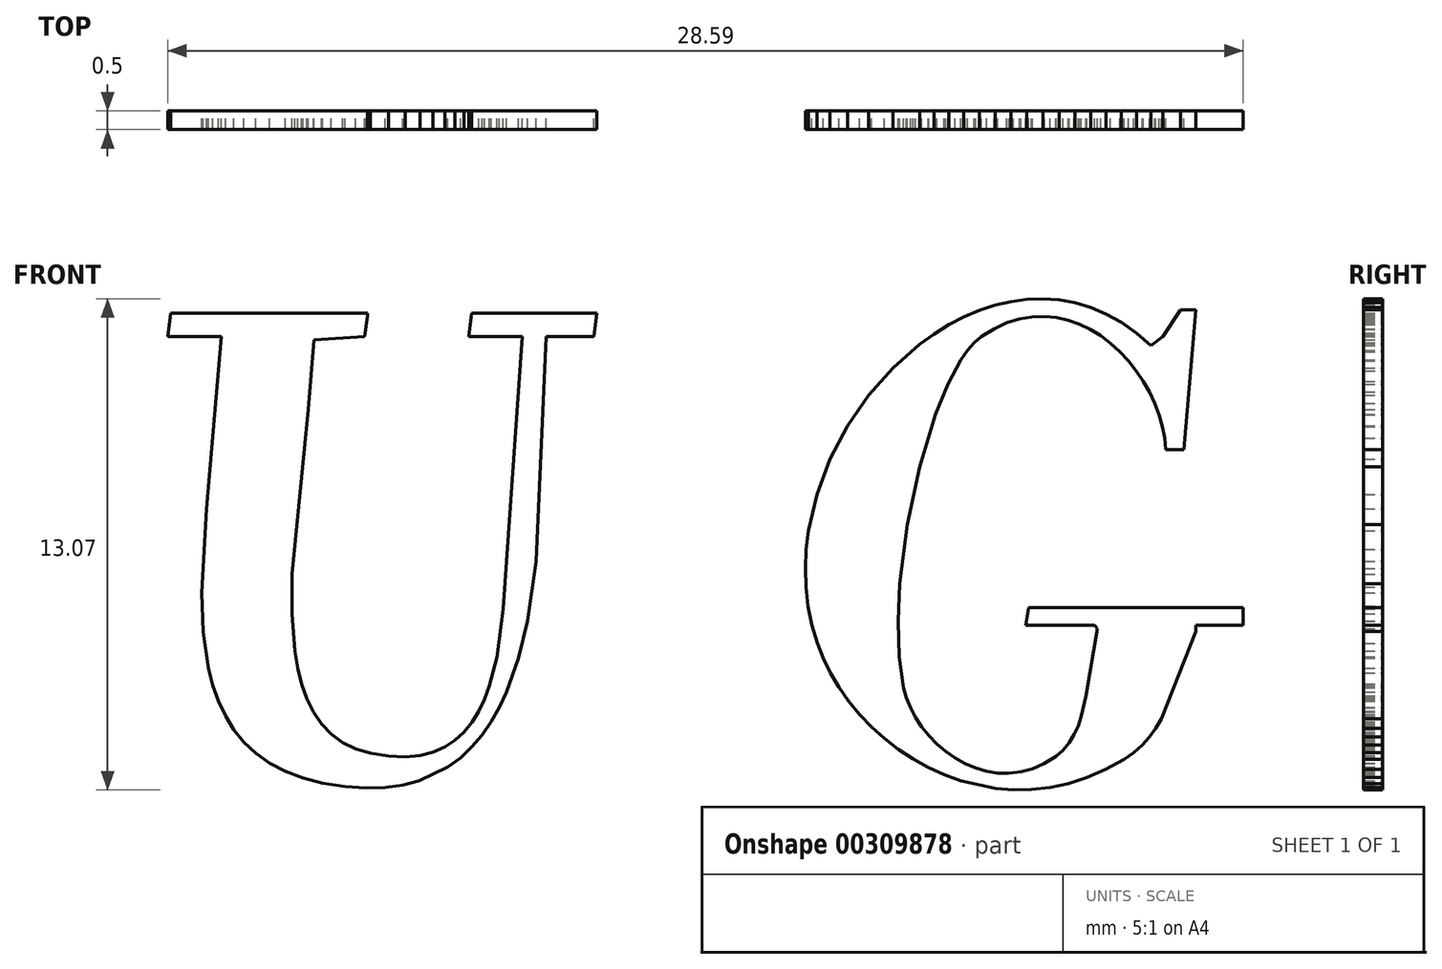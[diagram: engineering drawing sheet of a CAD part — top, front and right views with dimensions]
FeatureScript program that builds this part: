
annotation { "Feature Type Name" : "Feature", "Feature Type Description" : "" }
export const myFeature = defineFeature(function(context is Context, id is Id, definition is map)
    precondition{}
    {
        {
            var Q0;
            Q0=qCreatedBy(makeId("Front.planeOp"),FACE);
            var sketch = newSketch(context, id + "F0", { "sketchPlane" : qUnion([Q0])});
            skPoint(sketch, "E0.0", {"position": v(-16.68, 7.35) * mm});
            skPoint(sketch, "E1.0", {"position": v(-16.76, 6.72) * mm});
            skPoint(sketch, "E2.0", {"position": v(-15.33, 6.72) * mm});
            skPoint(sketch, "E3.0", {"position": v(-11.45, 7.35) * mm});
            skPoint(sketch, "E4.0", {"position": v(-11.45, 7.27) * mm});
            skPoint(sketch, "E5.0", {"position": v(-11.53, 6.72) * mm});
            skPoint(sketch, "E6.0", {"position": v(-12.88, 6.64) * mm});
            skPoint(sketch, "E7.0", {"position": v(-13.02, 4.78) * mm});
            skPoint(sketch, "E8.0", {"position": v(-13.46, 0.4) * mm});
            skPoint(sketch, "E9.0", {"position": v(-15.73, 2.14) * mm});
            skPoint(sketch, "E10.0", {"position": v(-15.86, -0.1) * mm});
            skPoint(sketch, "E11.0", {"position": v(-15.82, -1.14) * mm});
            skPoint(sketch, "E12.0", {"position": v(-13.46, -0.66) * mm});
            skPoint(sketch, "E13.0", {"position": v(-13.39, -1.64) * mm});
            skPoint(sketch, "E14.0", {"position": v(-15.68, -2.1) * mm});
            skPoint(sketch, "E15.0", {"position": v(-15.56, -2.55) * mm});
            skPoint(sketch, "E16.0", {"position": v(-13.3, -2.1) * mm});
            skPoint(sketch, "E17.0", {"position": v(-13.2, -2.52) * mm});
            skPoint(sketch, "E18.0", {"position": v(-15.41, -2.98) * mm});
            skPoint(sketch, "E19.0", {"position": v(-15.23, -3.37) * mm});
            skPoint(sketch, "E20.0", {"position": v(-13.06, -2.92) * mm});
            skPoint(sketch, "E21.0", {"position": v(-15, -3.74) * mm});
            skPoint(sketch, "E22.0", {"position": v(-14.73, -4.07) * mm});
            skPoint(sketch, "E23.0", {"position": v(-14.42, -4.37) * mm});
            skPoint(sketch, "E24.0", {"position": v(-14.05, -4.63) * mm});
            skPoint(sketch, "E25.0", {"position": v(-13.64, -4.85) * mm});
            skPoint(sketch, "E26.0", {"position": v(-13.17, -5.03) * mm});
            skPoint(sketch, "E27.0", {"position": v(-12.64, -5.16) * mm});
            skPoint(sketch, "E28.0", {"position": v(-12.88, -3.27) * mm});
            skPoint(sketch, "E29.0", {"position": v(-12.67, -3.59) * mm});
            skPoint(sketch, "E30.0", {"position": v(-12.41, -3.86) * mm});
            skPoint(sketch, "E31.0", {"position": v(-12.11, -4.08) * mm});
            skPoint(sketch, "E32.0", {"position": v(-12.05, -5.26) * mm});
            skPoint(sketch, "E33.0", {"position": v(-11.77, -4.25) * mm});
            skPoint(sketch, "E34.0", {"position": v(-11.5, -5.3) * mm});
            skPoint(sketch, "E35.0", {"position": v(-11.37, -4.37) * mm});
            skPoint(sketch, "E36.0", {"position": v(-10.89, -4.44) * mm});
            skPoint(sketch, "E37.0", {"position": v(-10.98, -5.28) * mm});
            skPoint(sketch, "E38.0", {"position": v(-10.45, -4.46) * mm});
            skPoint(sketch, "E39.0", {"position": v(-10.51, -5.21) * mm});
            skPoint(sketch, "E40.0", {"position": v(-10.08, -5.1) * mm});
            skPoint(sketch, "E41.0", {"position": v(-10.06, -4.42) * mm});
            skPoint(sketch, "E42.0", {"position": v(-9.7, -4.34) * mm});
            skPoint(sketch, "E43.0", {"position": v(-9.31, -4.73) * mm});
            skPoint(sketch, "E44.0", {"position": v(-9.4, -4.2) * mm});
            skPoint(sketch, "E45.0", {"position": v(-8.98, -4.49) * mm});
            skPoint(sketch, "E46.0", {"position": v(-9.12, -4.02) * mm});
            skPoint(sketch, "E47.0", {"position": v(-8.68, -4.2) * mm});
            skPoint(sketch, "E48.0", {"position": v(-8.88, -3.8) * mm});
            skPoint(sketch, "E49.0", {"position": v(-8.4, -3.88) * mm});
            skPoint(sketch, "E50.0", {"position": v(-8.67, -3.54) * mm});
            skPoint(sketch, "E51.0", {"position": v(-8.16, -3.53) * mm});
            skPoint(sketch, "E52.0", {"position": v(-8.5, -3.25) * mm});
            skPoint(sketch, "E53.0", {"position": v(-7.95, -3.15) * mm});
            skPoint(sketch, "E54.0", {"position": v(-8.34, -2.93) * mm});
            skPoint(sketch, "E55.0", {"position": v(-8.2, -2.58) * mm});
            skPoint(sketch, "E56.0", {"position": v(-7.75, -2.73) * mm});
            skPoint(sketch, "E57.0", {"position": v(-8.02, -1.8) * mm});
            skPoint(sketch, "E58.0", {"position": v(-7.44, -1.83) * mm});
            skPoint(sketch, "E59.0", {"position": v(-7.2, -0.85) * mm});
            skPoint(sketch, "E60.0", {"position": v(-7.85, -0.53) * mm});
            skPoint(sketch, "E61.0", {"position": v(-6.96, 0.75) * mm});
            skPoint(sketch, "E62.0", {"position": v(-6.7, 6.72) * mm});
            skPoint(sketch, "E63.0", {"position": v(-7.33, 6.72) * mm});
            skPoint(sketch, "E64.0", {"position": v(-8.76, 6.72) * mm});
            skPoint(sketch, "E65.0", {"position": v(-8.68, 7.35) * mm});
            skPoint(sketch, "E66.0", {"position": v(-5.35, 7.35) * mm});
            skPoint(sketch, "E67.0", {"position": v(-5.43, 6.72) * mm});
            skPoint(sketch, "E68.0", {"position": v(10.57, 7.43) * mm});
            skPoint(sketch, "E69.0", {"position": v(10.25, 3.7) * mm});
            skPoint(sketch, "E70.0", {"position": v(9.77, 3.7) * mm});
            skPoint(sketch, "E71.0", {"position": v(9.74, 4.02) * mm});
            skPoint(sketch, "E72.0", {"position": v(9.68, 4.33) * mm});
            skPoint(sketch, "E73.0", {"position": v(9.6, 4.64) * mm});
            skPoint(sketch, "E74.0", {"position": v(9.48, 4.95) * mm});
            skPoint(sketch, "E75.0", {"position": v(9.33, 5.25) * mm});
            skPoint(sketch, "E76.0", {"position": v(9.17, 5.54) * mm});
            skPoint(sketch, "E77.0", {"position": v(8.98, 5.82) * mm});
            skPoint(sketch, "E78.0", {"position": v(8.77, 6.08) * mm});
            skPoint(sketch, "E79.0", {"position": v(10.17, 7.43) * mm});
            skPoint(sketch, "E80.0", {"position": v(9.7, 6.72) * mm});
            skPoint(sketch, "E81.0", {"position": v(9.38, 6.48) * mm});
            skPoint(sketch, "E82.0", {"position": v(9, 6.82) * mm});
            skPoint(sketch, "E83.0", {"position": v(8.55, 6.32) * mm});
            skPoint(sketch, "E84.0", {"position": v(8.3, 6.55) * mm});
            skPoint(sketch, "E85.0", {"position": v(8.6, 7.1) * mm});
            skPoint(sketch, "E86.0", {"position": v(8.19, 7.33) * mm});
            skPoint(sketch, "E87.0", {"position": v(7.77, 6.91) * mm});
            skPoint(sketch, "E88.0", {"position": v(8.04, 6.74) * mm});
            skPoint(sketch, "E89.0", {"position": v(7.78, 7.5) * mm});
            skPoint(sketch, "E90.0", {"position": v(7.48, 7.05) * mm});
            skPoint(sketch, "E91.0", {"position": v(7.36, 7.63) * mm});
            skPoint(sketch, "E92.0", {"position": v(7.18, 7.16) * mm});
            skPoint(sketch, "E93.0", {"position": v(6.87, 7.23) * mm});
            skPoint(sketch, "E94.0", {"position": v(6.93, 7.7) * mm});
            skPoint(sketch, "E95.0", {"position": v(6.5, 7.73) * mm});
            skPoint(sketch, "E96.0", {"position": v(6.55, 7.26) * mm});
            skPoint(sketch, "E97.0", {"position": v(6.22, 7.25) * mm});
            skPoint(sketch, "E98.0", {"position": v(6.08, 7.71) * mm});
            skPoint(sketch, "E99.0", {"position": v(5.65, 7.66) * mm});
            skPoint(sketch, "E100.0", {"position": v(5.88, 7.2) * mm});
            skPoint(sketch, "E101.0", {"position": v(5.23, 7.56) * mm});
            skPoint(sketch, "E102.0", {"position": v(5.55, 7.09) * mm});
            skPoint(sketch, "E103.0", {"position": v(5.2, 6.93) * mm});
            skPoint(sketch, "E104.0", {"position": v(4.82, 7.42) * mm});
            skPoint(sketch, "E105.0", {"position": v(4.4, 7.25) * mm});
            skPoint(sketch, "E106.0", {"position": v(4.86, 6.72) * mm});
            skPoint(sketch, "E107.0", {"position": v(4.68, 6.56) * mm});
            skPoint(sketch, "E108.0", {"position": v(4, 7.04) * mm});
            skPoint(sketch, "E109.0", {"position": v(3.61, 6.8) * mm});
            skPoint(sketch, "E110.0", {"position": v(4.32, 6.1) * mm});
            skPoint(sketch, "E111.0", {"position": v(4.5, 6.36) * mm});
            skPoint(sketch, "E112.0", {"position": v(3.23, 6.52) * mm});
            skPoint(sketch, "E113.0", {"position": v(3.98, 5.45) * mm});
            skPoint(sketch, "E114.0", {"position": v(2.52, 5.89) * mm});
            skPoint(sketch, "E115.0", {"position": v(3.66, 4.65) * mm});
            skPoint(sketch, "E116.0", {"position": v(1.87, 5.16) * mm});
            skPoint(sketch, "E117.0", {"position": v(3.23, 3.26) * mm});
            skPoint(sketch, "E118.0", {"position": v(1.3, 4.34) * mm});
            skPoint(sketch, "E119.0", {"position": v(0.84, 3.46) * mm});
            skPoint(sketch, "E120.0", {"position": v(2.9, 1.72) * mm});
            skPoint(sketch, "E121.0", {"position": v(0.5, 2.52) * mm});
            skPoint(sketch, "E122.0", {"position": v(0.27, 1.55) * mm});
            skPoint(sketch, "E123.0", {"position": v(2.7, 0.15) * mm});
            skPoint(sketch, "E124.0", {"position": v(0.21, 1.05) * mm});
            skPoint(sketch, "E125.0", {"position": v(0.19, 0.55) * mm});
            skPoint(sketch, "E126.0", {"position": v(0.2, 0.05) * mm});
            skPoint(sketch, "E127.0", {"position": v(2.65, -0.86) * mm});
            skPoint(sketch, "E128.0", {"position": v(0.26, -0.45) * mm});
            skPoint(sketch, "E129.0", {"position": v(0.36, -0.94) * mm});
            skPoint(sketch, "E130.0", {"position": v(0.5, -1.44) * mm});
            skPoint(sketch, "E131.0", {"position": v(0.67, -1.84) * mm});
            skPoint(sketch, "E132.0", {"position": v(2.69, -1.8) * mm});
            skPoint(sketch, "E133.0", {"position": v(0.86, -2.23) * mm});
            skPoint(sketch, "E134.0", {"position": v(1.09, -2.62) * mm});
            skPoint(sketch, "E135.0", {"position": v(1.34, -2.98) * mm});
            skPoint(sketch, "E136.0", {"position": v(1.63, -3.33) * mm});
            skPoint(sketch, "E137.0", {"position": v(2.88, -2.9) * mm});
            skPoint(sketch, "E138.0", {"position": v(2.8, -2.63) * mm});
            skPoint(sketch, "E139.0", {"position": v(2.98, -3.16) * mm});
            skPoint(sketch, "E140.0", {"position": v(1.95, -3.66) * mm});
            skPoint(sketch, "E141.0", {"position": v(2.3, -3.97) * mm});
            skPoint(sketch, "E142.0", {"position": v(3.12, -3.41) * mm});
            skPoint(sketch, "E143.0", {"position": v(3.29, -3.66) * mm});
            skPoint(sketch, "E144.0", {"position": v(2.66, -4.26) * mm});
            skPoint(sketch, "E145.0", {"position": v(3.47, -3.9) * mm});
            skPoint(sketch, "E146.0", {"position": v(3.05, -4.52) * mm});
            skPoint(sketch, "E147.0", {"position": v(3.69, -4.12) * mm});
            skPoint(sketch, "E148.0", {"position": v(3.45, -4.74) * mm});
            skPoint(sketch, "E149.0", {"position": v(3.92, -4.32) * mm});
            skPoint(sketch, "E150.0", {"position": v(3.88, -4.94) * mm});
            skPoint(sketch, "E151.0", {"position": v(4.17, -4.5) * mm});
            skPoint(sketch, "E152.0", {"position": v(4.32, -5.1) * mm});
            skPoint(sketch, "E153.0", {"position": v(4.43, -4.64) * mm});
            skPoint(sketch, "E154.0", {"position": v(5, -4.84) * mm});
            skPoint(sketch, "E155.0", {"position": v(4.71, -4.76) * mm});
            skPoint(sketch, "E156.0", {"position": v(5.24, -5.3) * mm});
            skPoint(sketch, "E157.0", {"position": v(5.3, -4.9) * mm});
            skPoint(sketch, "E158.0", {"position": v(5.6, -4.9) * mm});
            skPoint(sketch, "E159.0", {"position": v(5.72, -5.34) * mm});
            skPoint(sketch, "E160.0", {"position": v(5.92, -4.86) * mm});
            skPoint(sketch, "E161.0", {"position": v(6.2, -5.33) * mm});
            skPoint(sketch, "E162.0", {"position": v(6.23, -4.78) * mm});
            skPoint(sketch, "E163.0", {"position": v(6.7, -5.28) * mm});
            skPoint(sketch, "E164.0", {"position": v(6.54, -4.64) * mm});
            skPoint(sketch, "E165.0", {"position": v(7.19, -5.17) * mm});
            skPoint(sketch, "E166.0", {"position": v(6.84, -4.45) * mm});
            skPoint(sketch, "E167.0", {"position": v(7.68, -5.01) * mm});
            skPoint(sketch, "E168.0", {"position": v(7.04, -4.28) * mm});
            skPoint(sketch, "E169.0", {"position": v(7.2, -4.09) * mm});
            skPoint(sketch, "E170.0", {"position": v(8.17, -4.8) * mm});
            skPoint(sketch, "E171.0", {"position": v(7.33, -3.87) * mm});
            skPoint(sketch, "E172.0", {"position": v(8.66, -4.53) * mm});
            skPoint(sketch, "E173.0", {"position": v(7.44, -3.64) * mm});
            skPoint(sketch, "E174.0", {"position": v(7.53, -3.39) * mm});
            skPoint(sketch, "E175.0", {"position": v(8.92, -4.35) * mm});
            skPoint(sketch, "E176.0", {"position": v(9.15, -4.15) * mm});
            skPoint(sketch, "E177.0", {"position": v(9.34, -3.93) * mm});
            skPoint(sketch, "E178.0", {"position": v(9.5, -3.7) * mm});
            skPoint(sketch, "E179.0", {"position": v(7.65, -2.84) * mm});
            skPoint(sketch, "E180.0", {"position": v(9.65, -3.45) * mm});
            skPoint(sketch, "E181.0", {"position": v(7.95, -1.04) * mm});
            skPoint(sketch, "E182.0", {"position": v(7.87, -0.96) * mm});
            skPoint(sketch, "E183.0", {"position": v(6.05, -0.96) * mm});
            skPoint(sketch, "E184.0", {"position": v(6.13, -0.49) * mm});
            skPoint(sketch, "E185.0", {"position": v(11.83, -0.49) * mm});
            skPoint(sketch, "E186.0", {"position": v(11.83, -0.96) * mm});
            skPoint(sketch, "E187.0", {"position": v(10.57, -0.96) * mm});
            skPoint(sketch, "E188.0", {"position": v(10.57, -1.12) * mm});
            skLineSegment(sketch, "E189", {"start": v(-16.68, 7.35) * mm, "end": v(-11.45, 7.35) * mm});
            skLineSegment(sketch, "E190", {"start": v(-11.45, 7.35) * mm, "end": v(-11.45, 7.27) * mm});
            skLineSegment(sketch, "E191", {"start": v(-11.45, 7.27) * mm, "end": v(-11.53, 6.72) * mm});
            skLineSegment(sketch, "E192", {"start": v(-11.53, 6.72) * mm, "end": v(-12.88, 6.64) * mm});
            skLineSegment(sketch, "E193", {"start": v(-12.88, 6.64) * mm, "end": v(-13.02, 4.78) * mm});
            skLineSegment(sketch, "E194", {"start": v(-13.02, 4.78) * mm, "end": v(-13.46, 0.4) * mm});
            skLineSegment(sketch, "E195", {"start": v(-13.46, 0.4) * mm, "end": v(-13.46, -0.66) * mm});
            skLineSegment(sketch, "E196", {"start": v(-13.46, -0.66) * mm, "end": v(-13.39, -1.64) * mm});
            skLineSegment(sketch, "E197", {"start": v(-13.39, -1.64) * mm, "end": v(-13.3, -2.1) * mm});
            skLineSegment(sketch, "E198", {"start": v(-13.3, -2.1) * mm, "end": v(-13.2, -2.52) * mm});
            skLineSegment(sketch, "E199", {"start": v(-13.2, -2.52) * mm, "end": v(-13.06, -2.92) * mm});
            skLineSegment(sketch, "E200", {"start": v(-13.06, -2.92) * mm, "end": v(-12.88, -3.27) * mm});
            skLineSegment(sketch, "E201", {"start": v(-12.88, -3.27) * mm, "end": v(-12.67, -3.59) * mm});
            skLineSegment(sketch, "E202", {"start": v(-12.67, -3.59) * mm, "end": v(-12.41, -3.86) * mm});
            skLineSegment(sketch, "E203", {"start": v(-12.41, -3.86) * mm, "end": v(-12.11, -4.08) * mm});
            skLineSegment(sketch, "E204", {"start": v(-12.11, -4.08) * mm, "end": v(-11.77, -4.25) * mm});
            skLineSegment(sketch, "E205", {"start": v(-11.77, -4.25) * mm, "end": v(-11.37, -4.37) * mm});
            skLineSegment(sketch, "E206", {"start": v(-11.37, -4.37) * mm, "end": v(-10.89, -4.44) * mm});
            skLineSegment(sketch, "E207", {"start": v(-10.89, -4.44) * mm, "end": v(-10.45, -4.46) * mm});
            skLineSegment(sketch, "E208", {"start": v(-10.45, -4.46) * mm, "end": v(-10.06, -4.42) * mm});
            skLineSegment(sketch, "E209", {"start": v(-10.06, -4.42) * mm, "end": v(-9.7, -4.34) * mm});
            skLineSegment(sketch, "E210", {"start": v(-9.7, -4.34) * mm, "end": v(-9.4, -4.2) * mm});
            skLineSegment(sketch, "E211", {"start": v(-9.4, -4.2) * mm, "end": v(-9.12, -4.02) * mm});
            skLineSegment(sketch, "E212", {"start": v(-9.12, -4.02) * mm, "end": v(-8.88, -3.8) * mm});
            skLineSegment(sketch, "E213", {"start": v(-8.88, -3.8) * mm, "end": v(-8.67, -3.54) * mm});
            skLineSegment(sketch, "E214", {"start": v(-8.67, -3.54) * mm, "end": v(-8.5, -3.25) * mm});
            skLineSegment(sketch, "E215", {"start": v(-8.5, -3.25) * mm, "end": v(-8.34, -2.93) * mm});
            skLineSegment(sketch, "E216", {"start": v(-8.34, -2.93) * mm, "end": v(-8.2, -2.58) * mm});
            skLineSegment(sketch, "E217", {"start": v(-8.2, -2.58) * mm, "end": v(-8.02, -1.8) * mm});
            skLineSegment(sketch, "E218", {"start": v(-8.02, -1.8) * mm, "end": v(-7.85, -0.53) * mm});
            skLineSegment(sketch, "E219", {"start": v(-7.85, -0.53) * mm, "end": v(-7.33, 6.72) * mm});
            skLineSegment(sketch, "E220", {"start": v(-7.33, 6.72) * mm, "end": v(-8.76, 6.72) * mm});
            skLineSegment(sketch, "E221", {"start": v(-8.76, 6.72) * mm, "end": v(-8.68, 7.35) * mm});
            skLineSegment(sketch, "E222", {"start": v(-8.68, 7.35) * mm, "end": v(-5.35, 7.35) * mm});
            skLineSegment(sketch, "E223", {"start": v(-5.35, 7.35) * mm, "end": v(-5.43, 6.72) * mm});
            skLineSegment(sketch, "E224", {"start": v(-5.43, 6.72) * mm, "end": v(-6.7, 6.72) * mm});
            skLineSegment(sketch, "E225", {"start": v(-6.7, 6.72) * mm, "end": v(-6.96, 0.75) * mm});
            skLineSegment(sketch, "E226", {"start": v(-6.96, 0.75) * mm, "end": v(-7.2, -0.85) * mm});
            skLineSegment(sketch, "E227", {"start": v(-7.2, -0.85) * mm, "end": v(-7.44, -1.83) * mm});
            skLineSegment(sketch, "E228", {"start": v(-7.44, -1.83) * mm, "end": v(-7.75, -2.73) * mm});
            skLineSegment(sketch, "E229", {"start": v(-7.75, -2.73) * mm, "end": v(-7.95, -3.15) * mm});
            skLineSegment(sketch, "E230", {"start": v(-7.95, -3.15) * mm, "end": v(-8.16, -3.53) * mm});
            skLineSegment(sketch, "E231", {"start": v(-8.16, -3.53) * mm, "end": v(-8.4, -3.88) * mm});
            skLineSegment(sketch, "E232", {"start": v(-8.4, -3.88) * mm, "end": v(-8.68, -4.2) * mm});
            skLineSegment(sketch, "E233", {"start": v(-8.68, -4.2) * mm, "end": v(-8.98, -4.49) * mm});
            skLineSegment(sketch, "E234", {"start": v(-8.98, -4.49) * mm, "end": v(-9.31, -4.73) * mm});
            skLineSegment(sketch, "E235", {"start": v(-9.31, -4.73) * mm, "end": v(-10.08, -5.1) * mm});
            skLineSegment(sketch, "E236", {"start": v(-10.08, -5.1) * mm, "end": v(-10.51, -5.21) * mm});
            skLineSegment(sketch, "E237", {"start": v(-10.51, -5.21) * mm, "end": v(-10.98, -5.28) * mm});
            skLineSegment(sketch, "E238", {"start": v(-10.98, -5.28) * mm, "end": v(-11.5, -5.3) * mm});
            skLineSegment(sketch, "E239", {"start": v(-11.5, -5.3) * mm, "end": v(-12.05, -5.26) * mm});
            skLineSegment(sketch, "E240", {"start": v(-12.05, -5.26) * mm, "end": v(-12.64, -5.16) * mm});
            skLineSegment(sketch, "E241", {"start": v(-12.64, -5.16) * mm, "end": v(-13.17, -5.03) * mm});
            skLineSegment(sketch, "E242", {"start": v(-13.17, -5.03) * mm, "end": v(-13.64, -4.85) * mm});
            skLineSegment(sketch, "E243", {"start": v(-13.64, -4.85) * mm, "end": v(-14.05, -4.63) * mm});
            skLineSegment(sketch, "E244", {"start": v(-14.05, -4.63) * mm, "end": v(-14.42, -4.37) * mm});
            skLineSegment(sketch, "E245", {"start": v(-14.42, -4.37) * mm, "end": v(-14.73, -4.07) * mm});
            skLineSegment(sketch, "E246", {"start": v(-14.73, -4.07) * mm, "end": v(-15, -3.74) * mm});
            skLineSegment(sketch, "E247", {"start": v(-15, -3.74) * mm, "end": v(-15.23, -3.37) * mm});
            skLineSegment(sketch, "E248", {"start": v(-15.23, -3.37) * mm, "end": v(-15.41, -2.98) * mm});
            skLineSegment(sketch, "E249", {"start": v(-15.41, -2.98) * mm, "end": v(-15.56, -2.55) * mm});
            skLineSegment(sketch, "E250", {"start": v(-15.56, -2.55) * mm, "end": v(-15.68, -2.1) * mm});
            skLineSegment(sketch, "E251", {"start": v(-15.68, -2.1) * mm, "end": v(-15.82, -1.14) * mm});
            skLineSegment(sketch, "E252", {"start": v(-15.82, -1.14) * mm, "end": v(-15.86, -0.1) * mm});
            skLineSegment(sketch, "E253", {"start": v(-15.86, -0.1) * mm, "end": v(-15.73, 2.14) * mm});
            skLineSegment(sketch, "E254", {"start": v(-15.73, 2.14) * mm, "end": v(-15.33, 6.72) * mm});
            skLineSegment(sketch, "E255", {"start": v(-15.33, 6.72) * mm, "end": v(-16.76, 6.72) * mm});
            skLineSegment(sketch, "E256", {"start": v(-16.76, 6.72) * mm, "end": v(-16.68, 7.35) * mm});
            skLineSegment(sketch, "E257", {"start": v(10.57, 7.43) * mm, "end": v(10.25, 3.7) * mm});
            skLineSegment(sketch, "E258", {"start": v(10.25, 3.7) * mm, "end": v(9.77, 3.7) * mm});
            skLineSegment(sketch, "E259", {"start": v(9.77, 3.7) * mm, "end": v(9.74, 4.02) * mm});
            skLineSegment(sketch, "E260", {"start": v(9.74, 4.02) * mm, "end": v(9.68, 4.33) * mm});
            skLineSegment(sketch, "E261", {"start": v(9.68, 4.33) * mm, "end": v(9.6, 4.64) * mm});
            skLineSegment(sketch, "E262", {"start": v(9.6, 4.64) * mm, "end": v(9.48, 4.95) * mm});
            skLineSegment(sketch, "E263", {"start": v(9.48, 4.95) * mm, "end": v(9.33, 5.25) * mm});
            skLineSegment(sketch, "E264", {"start": v(9.33, 5.25) * mm, "end": v(9.17, 5.54) * mm});
            skLineSegment(sketch, "E265", {"start": v(9.17, 5.54) * mm, "end": v(8.98, 5.82) * mm});
            skLineSegment(sketch, "E266", {"start": v(8.98, 5.82) * mm, "end": v(8.77, 6.08) * mm});
            skLineSegment(sketch, "E267", {"start": v(8.77, 6.08) * mm, "end": v(8.55, 6.32) * mm});
            skLineSegment(sketch, "E268", {"start": v(8.55, 6.32) * mm, "end": v(8.3, 6.55) * mm});
            skLineSegment(sketch, "E269", {"start": v(8.3, 6.55) * mm, "end": v(8.04, 6.74) * mm});
            skLineSegment(sketch, "E270", {"start": v(8.04, 6.74) * mm, "end": v(7.77, 6.91) * mm});
            skLineSegment(sketch, "E271", {"start": v(7.77, 6.91) * mm, "end": v(7.48, 7.05) * mm});
            skLineSegment(sketch, "E272", {"start": v(7.48, 7.05) * mm, "end": v(7.18, 7.16) * mm});
            skLineSegment(sketch, "E273", {"start": v(7.18, 7.16) * mm, "end": v(6.87, 7.23) * mm});
            skLineSegment(sketch, "E274", {"start": v(6.87, 7.23) * mm, "end": v(6.55, 7.26) * mm});
            skLineSegment(sketch, "E275", {"start": v(6.55, 7.26) * mm, "end": v(6.22, 7.25) * mm});
            skLineSegment(sketch, "E276", {"start": v(6.22, 7.25) * mm, "end": v(5.88, 7.2) * mm});
            skLineSegment(sketch, "E277", {"start": v(5.88, 7.2) * mm, "end": v(5.55, 7.09) * mm});
            skLineSegment(sketch, "E278", {"start": v(5.55, 7.09) * mm, "end": v(5.2, 6.93) * mm});
            skLineSegment(sketch, "E279", {"start": v(5.2, 6.93) * mm, "end": v(4.86, 6.72) * mm});
            skLineSegment(sketch, "E280", {"start": v(4.86, 6.72) * mm, "end": v(4.68, 6.56) * mm});
            skLineSegment(sketch, "E281", {"start": v(4.68, 6.56) * mm, "end": v(4.5, 6.36) * mm});
            skLineSegment(sketch, "E282", {"start": v(4.5, 6.36) * mm, "end": v(4.32, 6.1) * mm});
            skLineSegment(sketch, "E283", {"start": v(4.32, 6.1) * mm, "end": v(3.98, 5.45) * mm});
            skLineSegment(sketch, "E284", {"start": v(3.98, 5.45) * mm, "end": v(3.66, 4.65) * mm});
            skLineSegment(sketch, "E285", {"start": v(3.66, 4.65) * mm, "end": v(3.23, 3.26) * mm});
            skLineSegment(sketch, "E286", {"start": v(3.23, 3.26) * mm, "end": v(2.9, 1.72) * mm});
            skLineSegment(sketch, "E287", {"start": v(2.9, 1.72) * mm, "end": v(2.7, 0.15) * mm});
            skLineSegment(sketch, "E288", {"start": v(2.7, 0.15) * mm, "end": v(2.65, -0.86) * mm});
            skLineSegment(sketch, "E289", {"start": v(2.65, -0.86) * mm, "end": v(2.69, -1.8) * mm});
            skLineSegment(sketch, "E290", {"start": v(2.69, -1.8) * mm, "end": v(2.8, -2.63) * mm});
            skLineSegment(sketch, "E291", {"start": v(2.8, -2.63) * mm, "end": v(2.88, -2.9) * mm});
            skLineSegment(sketch, "E292", {"start": v(2.88, -2.9) * mm, "end": v(2.98, -3.16) * mm});
            skLineSegment(sketch, "E293", {"start": v(2.98, -3.16) * mm, "end": v(3.12, -3.41) * mm});
            skLineSegment(sketch, "E294", {"start": v(3.12, -3.41) * mm, "end": v(3.29, -3.66) * mm});
            skLineSegment(sketch, "E295", {"start": v(3.29, -3.66) * mm, "end": v(3.47, -3.9) * mm});
            skLineSegment(sketch, "E296", {"start": v(3.47, -3.9) * mm, "end": v(3.69, -4.12) * mm});
            skLineSegment(sketch, "E297", {"start": v(3.69, -4.12) * mm, "end": v(3.92, -4.32) * mm});
            skLineSegment(sketch, "E298", {"start": v(3.92, -4.32) * mm, "end": v(4.17, -4.5) * mm});
            skLineSegment(sketch, "E299", {"start": v(4.17, -4.5) * mm, "end": v(4.43, -4.64) * mm});
            skLineSegment(sketch, "E300", {"start": v(4.43, -4.64) * mm, "end": v(4.71, -4.76) * mm});
            skLineSegment(sketch, "E301", {"start": v(4.71, -4.76) * mm, "end": v(5, -4.84) * mm});
            skLineSegment(sketch, "E302", {"start": v(5, -4.84) * mm, "end": v(5.3, -4.9) * mm});
            skLineSegment(sketch, "E303", {"start": v(5.3, -4.9) * mm, "end": v(5.6, -4.9) * mm});
            skLineSegment(sketch, "E304", {"start": v(5.6, -4.9) * mm, "end": v(5.92, -4.86) * mm});
            skLineSegment(sketch, "E305", {"start": v(5.92, -4.86) * mm, "end": v(6.23, -4.78) * mm});
            skLineSegment(sketch, "E306", {"start": v(6.23, -4.78) * mm, "end": v(6.54, -4.64) * mm});
            skLineSegment(sketch, "E307", {"start": v(6.54, -4.64) * mm, "end": v(6.84, -4.45) * mm});
            skLineSegment(sketch, "E308", {"start": v(6.84, -4.45) * mm, "end": v(7.04, -4.28) * mm});
            skLineSegment(sketch, "E309", {"start": v(7.04, -4.28) * mm, "end": v(7.2, -4.09) * mm});
            skLineSegment(sketch, "E310", {"start": v(7.2, -4.09) * mm, "end": v(7.33, -3.87) * mm});
            skLineSegment(sketch, "E311", {"start": v(7.33, -3.87) * mm, "end": v(7.44, -3.64) * mm});
            skLineSegment(sketch, "E312", {"start": v(7.44, -3.64) * mm, "end": v(7.53, -3.39) * mm});
            skLineSegment(sketch, "E313", {"start": v(7.53, -3.39) * mm, "end": v(7.65, -2.84) * mm});
            skLineSegment(sketch, "E314", {"start": v(7.65, -2.84) * mm, "end": v(7.95, -1.04) * mm});
            skLineSegment(sketch, "E315", {"start": v(7.95, -1.04) * mm, "end": v(7.87, -0.96) * mm});
            skLineSegment(sketch, "E316", {"start": v(7.87, -0.96) * mm, "end": v(6.05, -0.96) * mm});
            skLineSegment(sketch, "E317", {"start": v(6.05, -0.96) * mm, "end": v(6.13, -0.49) * mm});
            skLineSegment(sketch, "E318", {"start": v(6.13, -0.49) * mm, "end": v(11.83, -0.49) * mm});
            skLineSegment(sketch, "E319", {"start": v(11.83, -0.49) * mm, "end": v(11.83, -0.96) * mm});
            skLineSegment(sketch, "E320", {"start": v(11.83, -0.96) * mm, "end": v(10.57, -0.96) * mm});
            skLineSegment(sketch, "E321", {"start": v(10.57, -0.96) * mm, "end": v(10.57, -1.12) * mm});
            skLineSegment(sketch, "E322", {"start": v(10.57, -1.12) * mm, "end": v(9.65, -3.45) * mm});
            skLineSegment(sketch, "E323", {"start": v(9.65, -3.45) * mm, "end": v(9.5, -3.7) * mm});
            skLineSegment(sketch, "E324", {"start": v(9.5, -3.7) * mm, "end": v(9.34, -3.93) * mm});
            skLineSegment(sketch, "E325", {"start": v(9.34, -3.93) * mm, "end": v(9.15, -4.15) * mm});
            skLineSegment(sketch, "E326", {"start": v(9.15, -4.15) * mm, "end": v(8.92, -4.35) * mm});
            skLineSegment(sketch, "E327", {"start": v(8.92, -4.35) * mm, "end": v(8.66, -4.53) * mm});
            skLineSegment(sketch, "E328", {"start": v(8.66, -4.53) * mm, "end": v(8.17, -4.8) * mm});
            skLineSegment(sketch, "E329", {"start": v(8.17, -4.8) * mm, "end": v(7.68, -5.01) * mm});
            skLineSegment(sketch, "E330", {"start": v(7.68, -5.01) * mm, "end": v(7.19, -5.17) * mm});
            skLineSegment(sketch, "E331", {"start": v(7.19, -5.17) * mm, "end": v(6.7, -5.28) * mm});
            skLineSegment(sketch, "E332", {"start": v(6.7, -5.28) * mm, "end": v(6.2, -5.33) * mm});
            skLineSegment(sketch, "E333", {"start": v(6.2, -5.33) * mm, "end": v(5.72, -5.34) * mm});
            skLineSegment(sketch, "E334", {"start": v(5.72, -5.34) * mm, "end": v(5.24, -5.3) * mm});
            skLineSegment(sketch, "E335", {"start": v(5.24, -5.3) * mm, "end": v(4.32, -5.1) * mm});
            skLineSegment(sketch, "E336", {"start": v(4.32, -5.1) * mm, "end": v(3.88, -4.94) * mm});
            skLineSegment(sketch, "E337", {"start": v(3.88, -4.94) * mm, "end": v(3.45, -4.74) * mm});
            skLineSegment(sketch, "E338", {"start": v(3.45, -4.74) * mm, "end": v(3.05, -4.52) * mm});
            skLineSegment(sketch, "E339", {"start": v(3.05, -4.52) * mm, "end": v(2.66, -4.26) * mm});
            skLineSegment(sketch, "E340", {"start": v(2.66, -4.26) * mm, "end": v(2.3, -3.97) * mm});
            skLineSegment(sketch, "E341", {"start": v(2.3, -3.97) * mm, "end": v(1.95, -3.66) * mm});
            skLineSegment(sketch, "E342", {"start": v(1.95, -3.66) * mm, "end": v(1.63, -3.33) * mm});
            skLineSegment(sketch, "E343", {"start": v(1.63, -3.33) * mm, "end": v(1.34, -2.98) * mm});
            skLineSegment(sketch, "E344", {"start": v(1.34, -2.98) * mm, "end": v(1.09, -2.62) * mm});
            skLineSegment(sketch, "E345", {"start": v(1.09, -2.62) * mm, "end": v(0.86, -2.23) * mm});
            skLineSegment(sketch, "E346", {"start": v(0.86, -2.23) * mm, "end": v(0.67, -1.84) * mm});
            skLineSegment(sketch, "E347", {"start": v(0.67, -1.84) * mm, "end": v(0.5, -1.44) * mm});
            skLineSegment(sketch, "E348", {"start": v(0.5, -1.44) * mm, "end": v(0.36, -0.94) * mm});
            skLineSegment(sketch, "E349", {"start": v(0.36, -0.94) * mm, "end": v(0.26, -0.45) * mm});
            skLineSegment(sketch, "E350", {"start": v(0.26, -0.45) * mm, "end": v(0.2, 0.05) * mm});
            skLineSegment(sketch, "E351", {"start": v(0.2, 0.05) * mm, "end": v(0.19, 0.55) * mm});
            skLineSegment(sketch, "E352", {"start": v(0.19, 0.55) * mm, "end": v(0.21, 1.05) * mm});
            skLineSegment(sketch, "E353", {"start": v(0.21, 1.05) * mm, "end": v(0.27, 1.55) * mm});
            skLineSegment(sketch, "E354", {"start": v(0.27, 1.55) * mm, "end": v(0.5, 2.52) * mm});
            skLineSegment(sketch, "E355", {"start": v(0.5, 2.52) * mm, "end": v(0.84, 3.46) * mm});
            skLineSegment(sketch, "E356", {"start": v(0.84, 3.46) * mm, "end": v(1.3, 4.34) * mm});
            skLineSegment(sketch, "E357", {"start": v(1.3, 4.34) * mm, "end": v(1.87, 5.16) * mm});
            skLineSegment(sketch, "E358", {"start": v(1.87, 5.16) * mm, "end": v(2.52, 5.89) * mm});
            skLineSegment(sketch, "E359", {"start": v(2.52, 5.89) * mm, "end": v(3.23, 6.52) * mm});
            skLineSegment(sketch, "E360", {"start": v(3.23, 6.52) * mm, "end": v(3.61, 6.8) * mm});
            skLineSegment(sketch, "E361", {"start": v(3.61, 6.8) * mm, "end": v(4, 7.04) * mm});
            skLineSegment(sketch, "E362", {"start": v(4, 7.04) * mm, "end": v(4.4, 7.25) * mm});
            skLineSegment(sketch, "E363", {"start": v(4.4, 7.25) * mm, "end": v(4.82, 7.42) * mm});
            skLineSegment(sketch, "E364", {"start": v(4.82, 7.42) * mm, "end": v(5.23, 7.56) * mm});
            skLineSegment(sketch, "E365", {"start": v(5.23, 7.56) * mm, "end": v(5.65, 7.66) * mm});
            skLineSegment(sketch, "E366", {"start": v(5.65, 7.66) * mm, "end": v(6.08, 7.71) * mm});
            skLineSegment(sketch, "E367", {"start": v(6.08, 7.71) * mm, "end": v(6.5, 7.73) * mm});
            skLineSegment(sketch, "E368", {"start": v(6.5, 7.73) * mm, "end": v(6.93, 7.7) * mm});
            skLineSegment(sketch, "E369", {"start": v(6.93, 7.7) * mm, "end": v(7.36, 7.63) * mm});
            skLineSegment(sketch, "E370", {"start": v(7.36, 7.63) * mm, "end": v(7.78, 7.5) * mm});
            skLineSegment(sketch, "E371", {"start": v(7.78, 7.5) * mm, "end": v(8.19, 7.33) * mm});
            skLineSegment(sketch, "E372", {"start": v(8.19, 7.33) * mm, "end": v(8.6, 7.1) * mm});
            skLineSegment(sketch, "E373", {"start": v(8.6, 7.1) * mm, "end": v(9, 6.82) * mm});
            skLineSegment(sketch, "E374", {"start": v(9, 6.82) * mm, "end": v(9.38, 6.48) * mm});
            skLineSegment(sketch, "E375", {"start": v(9.38, 6.48) * mm, "end": v(9.7, 6.72) * mm});
            skLineSegment(sketch, "E376", {"start": v(9.7, 6.72) * mm, "end": v(10.17, 7.43) * mm});
            skLineSegment(sketch, "E377", {"start": v(10.17, 7.43) * mm, "end": v(10.57, 7.43) * mm});
            skSolve(sketch);
        }
        {
            var Q0;
            Q0=makeQuery(id+"F0.imprint","IMPRINT",FACE,{"disambiguationData":[TD([[makeQuery(id+"F0.imprint","IMPRINT",EDGE,{"derivedFrom":sQuery(id+"F0.wireOp",EDGE,"E189")}),-1.0]])]});
            var Q1;
            Q1=makeQuery(id+"F0.imprint","IMPRINT",FACE,{"disambiguationData":[TD([[makeQuery(id+"F0.imprint","IMPRINT",EDGE,{"derivedFrom":sQuery(id+"F0.wireOp",EDGE,"E257")}),-1.0]])]});
            extrude(context, id + "F1", {"entities" : qUnion([Q0, Q1]), "depth" : 0.5 * mm});
        }
    });
